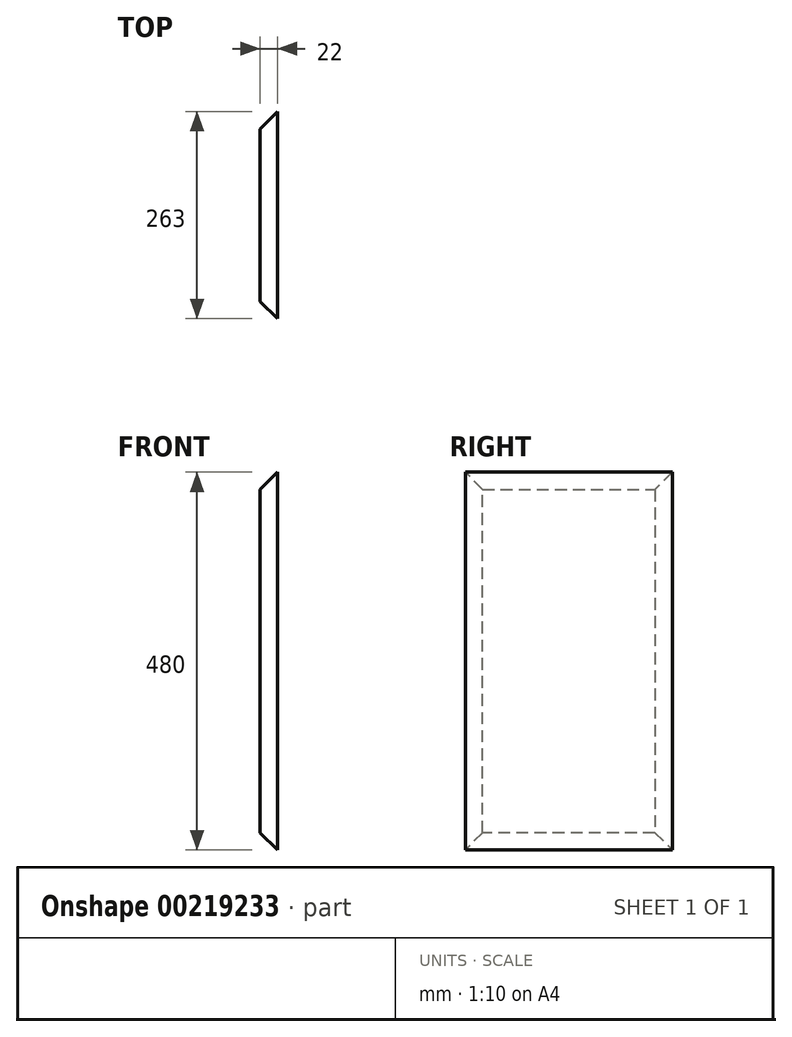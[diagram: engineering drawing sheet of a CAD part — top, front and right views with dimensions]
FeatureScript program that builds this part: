
annotation { "Feature Type Name" : "Feature", "Feature Type Description" : "" }
export const myFeature = defineFeature(function(context is Context, id is Id, definition is map)
    precondition{}
    {
        {
            var Q0;
            Q0=qCreatedBy(makeId("Right.planeOp"),FACE);
            var sketch = newSketch(context, id + "F0", { "sketchPlane" : qUnion([Q0])});
            skLineSegment(sketch, "E0.bottom", {"start": v(131.5, 240) * mm, "end": v(-131.5, 240) * mm});
            skLineSegment(sketch, "E0.top", {"start": v(131.5, -240) * mm, "end": v(-131.5, -240) * mm});
            skLineSegment(sketch, "E0.left", {"start": v(131.5, 240) * mm, "end": v(131.5, -240) * mm});
            skLineSegment(sketch, "E0.right", {"start": v(-131.5, 240) * mm, "end": v(-131.5, -240) * mm});
            skPoint(sketch, "E0.middle", {"position": v(0, 0) * mm});
            skSolve(sketch);
        }
        {
            var Q0;
            Q0 = qSketchRegion(id + "F0", true);
            extrude(context, id + "F1", {"entities" : qUnion([Q0]), "depth" : 22 * mm});
        }
        {
            var Q0;
            Q0=makeQuery(id+"F1.opExtrude","CAP_EDGE",EDGE,{"disambiguationData":[OSD([sQuery(id+"F0.wireOp",EDGE,"E0.left")])],"isStart":true});
            var Q1;
            Q1=makeQuery(id+"F1.opExtrude","CAP_EDGE",EDGE,{"disambiguationData":[OSD([sQuery(id+"F0.wireOp",EDGE,"E0.bottom")])],"isStart":true});
            var Q2;
            Q2=makeQuery(id+"F1.opExtrude","CAP_EDGE",EDGE,{"disambiguationData":[OSD([sQuery(id+"F0.wireOp",EDGE,"E0.right")])],"isStart":true});
            var Q3;
            Q3=makeQuery(id+"F1.opExtrude","CAP_EDGE",EDGE,{"disambiguationData":[OSD([sQuery(id+"F0.wireOp",EDGE,"E0.top")])],"isStart":true});
            chamfer(context, id + "F2", {"entities" : qUnion([Q0, Q1, Q2, Q3]), "width" : 22 * mm, "tangentPropagation" : true});
        }
    });
